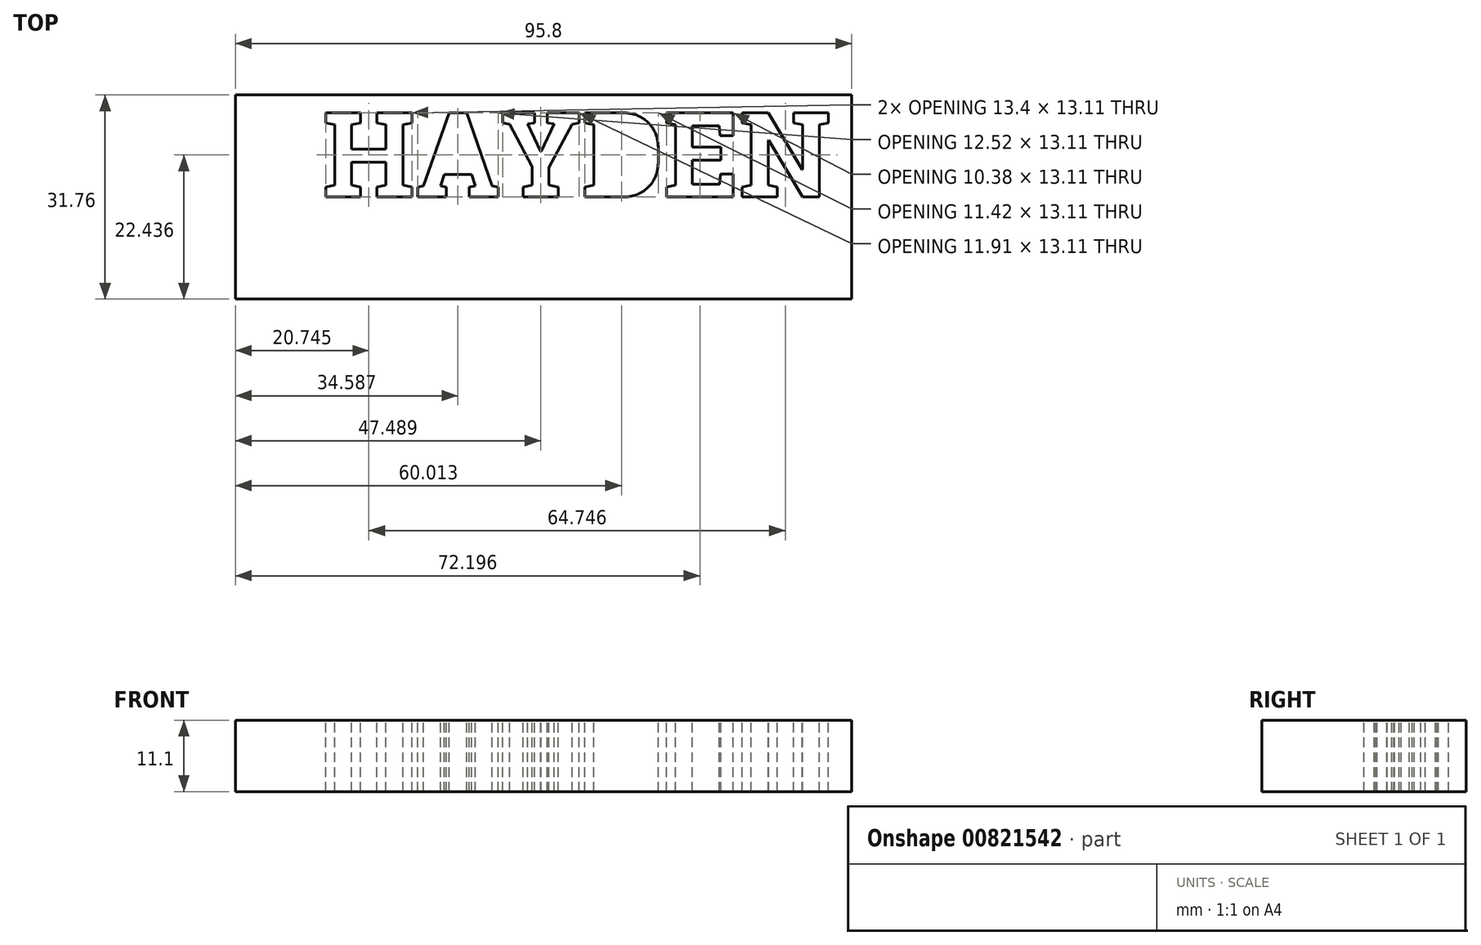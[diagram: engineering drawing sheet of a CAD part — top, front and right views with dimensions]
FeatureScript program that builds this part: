
annotation { "Feature Type Name" : "Feature", "Feature Type Description" : "" }
export const myFeature = defineFeature(function(context is Context, id is Id, definition is map)
    precondition{}
    {
        {
            var Q0;
            Q0=qCreatedBy(makeId("Top.planeOp"),FACE);
            var sketch = newSketch(context, id + "F0", { "sketchPlane" : qUnion([Q0])});
            skLineSegment(sketch, "E0.bottom", {"start": v(-48.81, 15.88) * mm, "end": v(46.99, 15.88) * mm});
            skLineSegment(sketch, "E0.top", {"start": v(-48.81, -15.88) * mm, "end": v(46.99, -15.88) * mm});
            skLineSegment(sketch, "E0.left", {"start": v(-48.81, 15.88) * mm, "end": v(-48.81, -15.88) * mm});
            skLineSegment(sketch, "E0.right", {"start": v(46.99, 15.88) * mm, "end": v(46.99, -15.88) * mm});
            skText(sketch, "E1", { "text": "HAYDEN", "fontName": "RobotoSlab-Bold.ttf"});
            const initialGuessF0  = {"E1": [-0.03527, 0, 1, 0, 0.01328]};
            skSetInitialGuess(sketch, initialGuessF0);
            skSolve(sketch);
        }
        {
            var Q0;
            Q0 = qSketchRegion(id + "F0", true);
            extrude(context, id + "F1", {"entities" : qUnion([Q0]), "oppositeDirection" : true, "depth" : 11.1 * mm, "offsetDistance" : 25 * mm});
        }
    });
